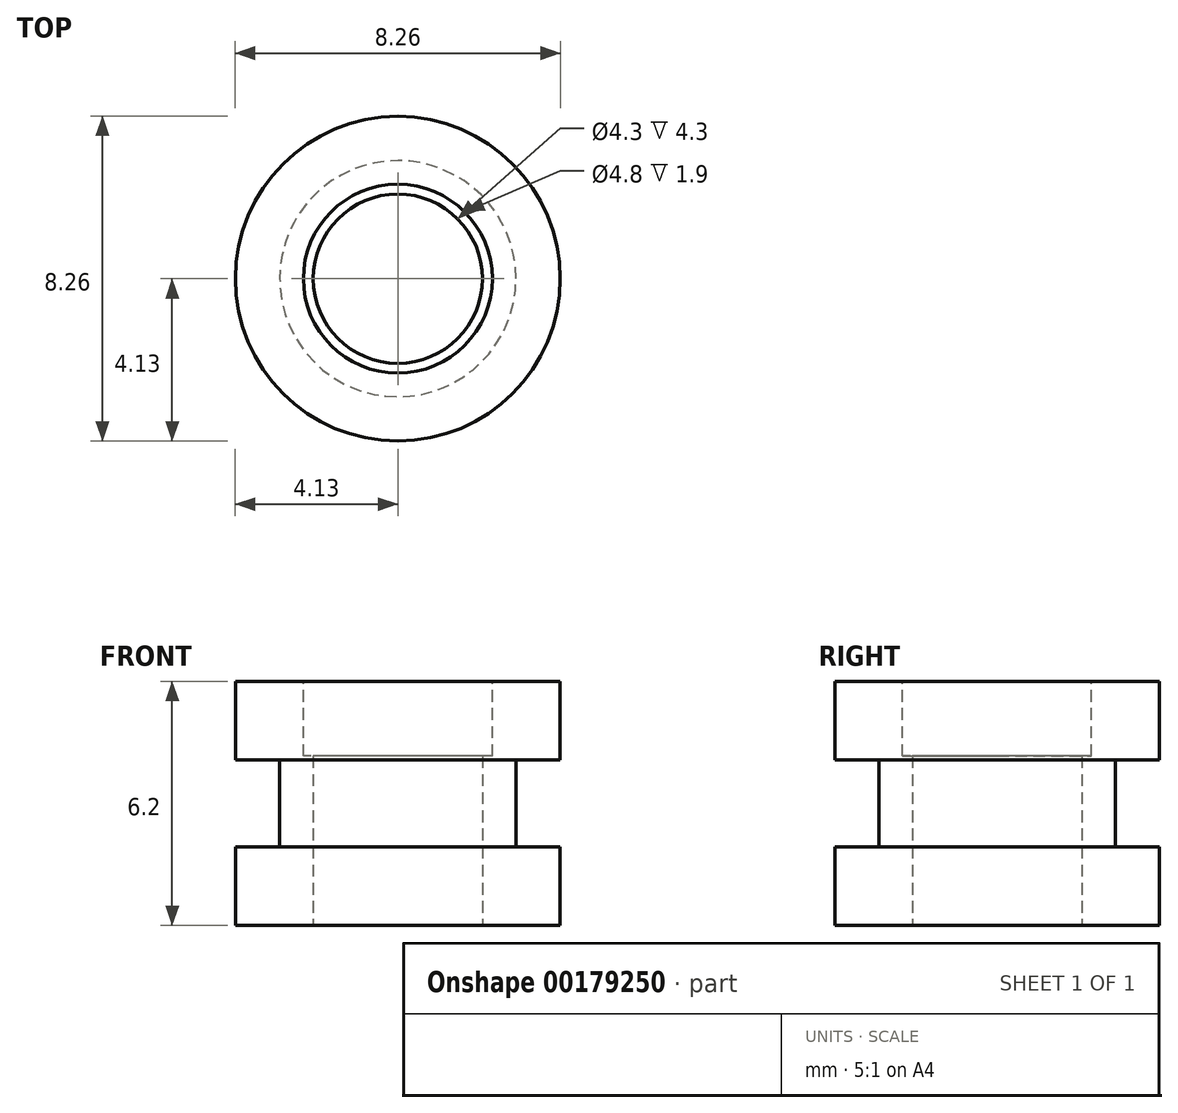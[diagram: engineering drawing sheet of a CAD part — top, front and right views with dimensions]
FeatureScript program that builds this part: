
annotation { "Feature Type Name" : "Feature", "Feature Type Description" : "" }
export const myFeature = defineFeature(function(context is Context, id is Id, definition is map)
    precondition{}
    {
        {
            var Q0;
            Q0=qCreatedBy(makeId("Top.planeOp"),FACE);
            var sketch = newSketch(context, id + "F0", { "sketchPlane" : qUnion([Q0])});
            skCircle(sketch, "E0", {"center": v(0, 0) * mm, "radius": 4.12 * mm});
            skCircle(sketch, "E1", {"center": v(0, 0) * mm, "radius": 2.15 * mm});
            skCircle(sketch, "E2", {"center": v(0, 0) * mm, "radius": 3 * mm});
            skSolve(sketch);
        }
        {
            var Q0;
            Q0=makeQuery(id+"F0.imprint","IMPRINT",FACE,{"disambiguationData":[TD([[makeQuery(id+"F0.imprint","IMPRINT",EDGE,{"derivedFrom":sQuery(id+"F0.wireOp",EDGE,"E0")}),1.0]])]});
            extrude(context, id + "F1", {"entities" : qUnion([Q0]), "depth" : 2 * mm});
        }
        {
            var Q0;
            Q0=makeQuery(id+"F0.imprint","IMPRINT",FACE,{"disambiguationData":[TD([[makeQuery(id+"F0.imprint","IMPRINT",EDGE,{"derivedFrom":sQuery(id+"F0.wireOp",EDGE,"E1")}),-1.0]])]});
            extrude(context, id + "F2", {"entities" : qUnion([Q0]), "operationType" : NewBodyOperationType.ADD, "depth" : 6.2 * mm});
        }
        {
            var Q0;
            Q0=makeQuery(id+"F2.opExtrude","CAP_FACE",FACE,{"disambiguationData":[OSD([sQuery(id+"F0.wireOp",EDGE,"E1"),sQuery(id+"F0.wireOp",EDGE,"E2")])],"isStart":false});
            var sketch = newSketch(context, id + "F3", { "sketchPlane" : qUnion([Q0])});
            skCircle(sketch, "E3", {"center": v(0, 0) * mm, "radius": 4.12 * mm});
            skCircle(sketch, "E4", {"center": v(0, 0) * mm, "radius": 2.4 * mm});
            skSolve(sketch);
        }
        {
            var Q0;
            Q0=makeQuery(id+"F3.imprint","IMPRINT",FACE,{"disambiguationData":[TD([[makeQuery(id+"F3.imprint","IMPRINT",EDGE,{"derivedFrom":sQuery(id+"F3.wireOp",EDGE,"E3")}),1.0]])]});
            extrude(context, id + "F4", {"entities" : qUnion([Q0]), "operationType" : NewBodyOperationType.ADD, "oppositeDirection" : true, "depth" : 2 * mm});
        }
        {
            var Q0;
            Q0=makeQuery(id+"F3.imprint","IMPRINT",FACE,{"disambiguationData":[TD([[makeQuery(id+"F3.imprint","IMPRINT",EDGE,{"derivedFrom":sQuery(id+"F3.wireOp",EDGE,"E4")}),1.0]])]});
            var Q1;
            Q1=makeQuery(id+"F3.imprint","IMPRINT",FACE,{"disambiguationData":[TD([[makeQuery(id+"F3.imprint","IMPRINT",EDGE,{"derivedFrom":makeQuery(id+"F2.opExtrude","CAP_EDGE",EDGE,{"disambiguationData":[OSD([sQuery(id+"F0.wireOp",EDGE,"E1")])],"isStart":false})}),1.0]])]});
            extrude(context, id + "F5", {"entities" : qUnion([Q0, Q1]), "operationType" : NewBodyOperationType.REMOVE, "oppositeDirection" : true, "depth" : 1.9 * mm});
        }
    });
